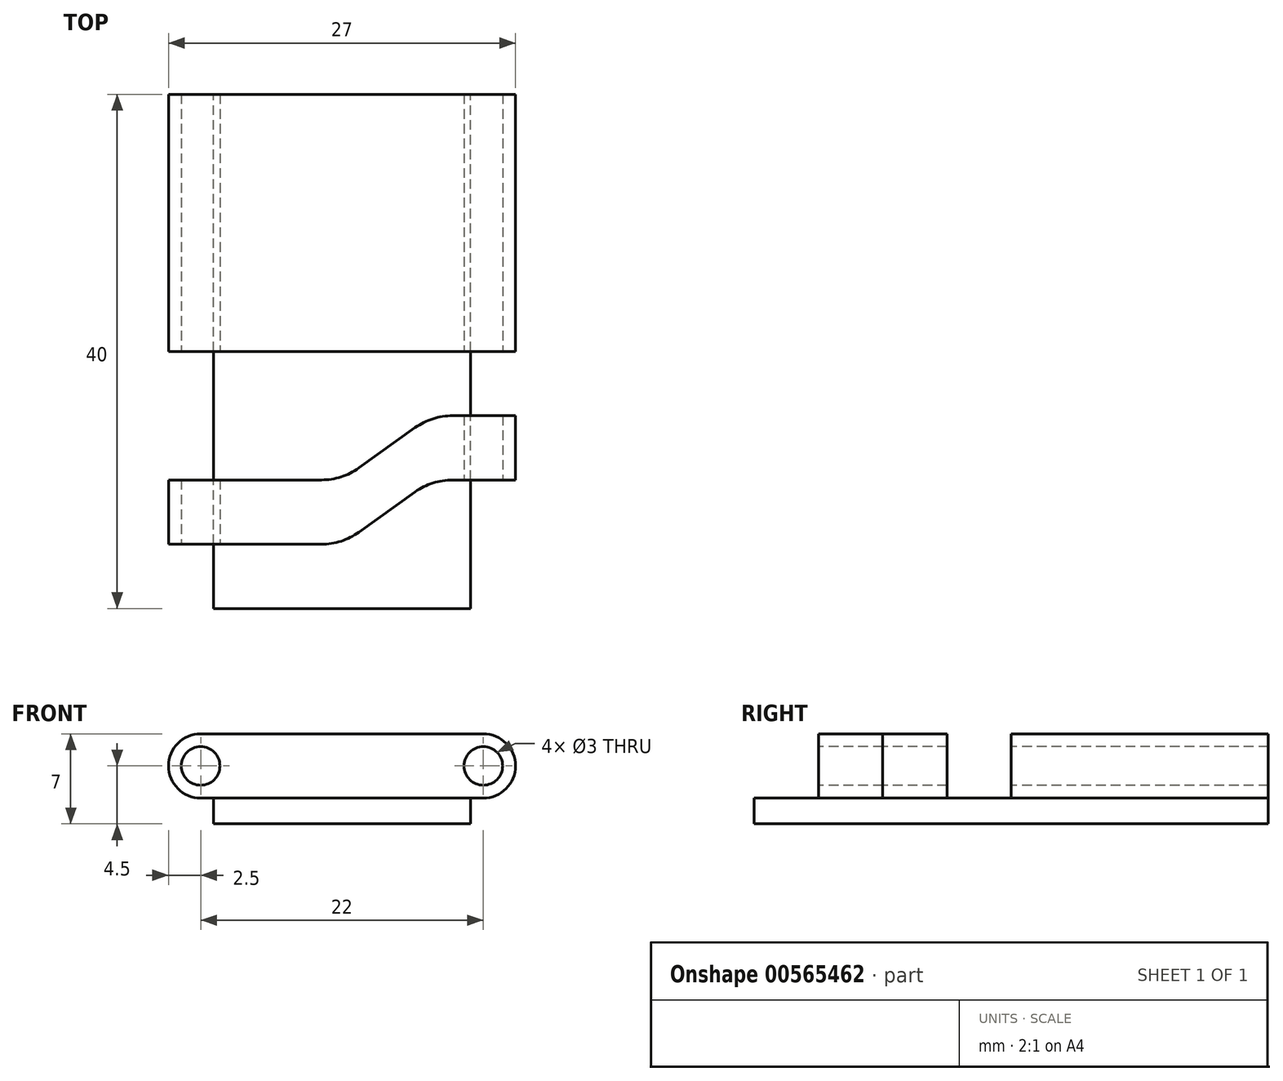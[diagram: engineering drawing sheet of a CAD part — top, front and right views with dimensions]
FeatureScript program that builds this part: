
annotation { "Feature Type Name" : "Feature", "Feature Type Description" : "" }
export const myFeature = defineFeature(function(context is Context, id is Id, definition is map)
    precondition{}
    {
        {
            var Q0;
            Q0=qCreatedBy(makeId("Front.planeOp"),FACE);
            var sketch = newSketch(context, id + "F0", { "sketchPlane" : qUnion([Q0])});
            skLineSegment(sketch, "E0.bottom", {"start": v(-10, 0) * mm, "end": v(10, 0) * mm});
            skLineSegment(sketch, "E0.top", {"start": v(-10, -1) * mm, "end": v(10, -1) * mm});
            skLineSegment(sketch, "E0.left", {"start": v(-10, 0) * mm, "end": v(-10, -1) * mm});
            skLineSegment(sketch, "E0.right", {"start": v(10, 0) * mm, "end": v(10, -1) * mm});
            skPoint(sketch, "E1", {"position": v(0, 0) * mm});
            skSolve(sketch);
        }
        {
            var Q0;
            Q0 = qSketchRegion(id + "F0", true);
            extrude(context, id + "F1", {"entities" : qUnion([Q0]), "depth" : 20 * mm, "offsetDistance" : 25 * mm, "hasSecondDirection" : true, "secondDirectionOppositeDirection" : true, "secondDirectionDepth" : 20 * mm});
        }
        {
            var Q0;
            Q0=makeQuery(id+"F1.opExtrude","CAP_FACE",FACE,{"disambiguationData":[OSD([sQuery(id+"F0.wireOp",EDGE,"E0.bottom"),sQuery(id+"F0.wireOp",EDGE,"E0.top"),sQuery(id+"F0.wireOp",EDGE,"E0.left"),sQuery(id+"F0.wireOp",EDGE,"E0.right")])],"isStart":true});
            var sketch = newSketch(context, id + "F2", { "sketchPlane" : qUnion([Q0])});
            skArc(sketch, "E2", {"start": v(11, 1) * mm, "mid": v(13.5, 3.5) * mm, "end": v(11, 6) * mm});
            skLineSegment(sketch, "E3", {"start": v(11, 1) * mm, "end": v(10, 1) * mm});
            skLineSegment(sketch, "E4", {"start": v(10, 1) * mm, "end": v(10, 0) * mm});
            skLineSegment(sketch, "E5", {"start": v(11, 3.5) * mm, "end": v(11, 1) * mm, "construction": true});
            skLineSegment(sketch, "E6", {"start": v(11, 6) * mm, "end": v(0, 6) * mm});
            skLineSegment(sketch, "E7", {"start": v(11, 3.5) * mm, "end": v(11, 6) * mm, "construction": true});
            skLineSegment(sketch, "E8", {"start": v(0, 0) * mm, "end": v(0, 10.25) * mm, "construction": true});
            skLineSegment(sketch, "E9", {"start": v(0, 0) * mm, "end": v(10, 0) * mm});
            skLineSegment(sketch, "E10.MirrorCS", {"start": v(-11, 6) * mm, "end": v(0, 6) * mm});
            skLineSegment(sketch, "E11.MirrorCS", {"start": v(-11, 3.5) * mm, "end": v(-11, 1) * mm, "construction": true});
            skLineSegment(sketch, "E12.MirrorCS", {"start": v(-11, 3.5) * mm, "end": v(-11, 6) * mm, "construction": true});
            skLineSegment(sketch, "E13.MirrorCS", {"start": v(0, 0) * mm, "end": v(-10, 0) * mm});
            skLineSegment(sketch, "E14.MirrorCS", {"start": v(-11, 1) * mm, "end": v(-10, 1) * mm});
            skLineSegment(sketch, "E15.MirrorCS", {"start": v(-10, 1) * mm, "end": v(-10, 0) * mm});
            skArc(sketch, "E16.MirrorCS", {"start": v(-11, 1) * mm, "mid": v(-13.5, 3.5) * mm, "end": v(-11, 6) * mm});
            skSolve(sketch);
        }
        {
            var Q0;
            Q0 = qSketchRegion(id + "F2", true);
            var Q1;
            Q1=makeQuery(id+"F1.opExtrude","CAP_FACE",FACE,{"disambiguationData":[OSD([sQuery(id+"F0.wireOp",EDGE,"E0.bottom"),sQuery(id+"F0.wireOp",EDGE,"E0.top"),sQuery(id+"F0.wireOp",EDGE,"E0.left"),sQuery(id+"F0.wireOp",EDGE,"E0.right")])],"isStart":false});
            extrude(context, id + "F3", {"entities" : qUnion([Q0]), "operationType" : NewBodyOperationType.ADD, "endBound" : BoundingType.UP_TO_SURFACE, "oppositeDirection" : true, "depth" : 25 * mm, "endBoundEntityFace" : qUnion([Q1]), "offsetDistance" : 25 * mm});
        }
        {
            var Q0;
            Q0=makeQuery(id+"F3.opExtrude","SWEPT_FACE",FACE,{"disambiguationData":[OSD([sQuery(id+"F2.wireOp",EDGE,"E6"),sQuery(id+"F2.wireOp",EDGE,"E10.MirrorCS")])]});
            var sketch = newSketch(context, id + "F4", { "sketchPlane" : qUnion([Q0])});
            skLineSegment(sketch, "E17", {"start": v(-19.6, 0) * mm, "end": v(21.58, 0) * mm, "construction": true});
            skPoint(sketch, "E17.endSnap0", {"position": v(-11, 0) * mm});
            skLineSegment(sketch, "E18", {"start": v(-16.8, -15) * mm, "end": v(16.67, -15) * mm, "construction": true});
            skPoint(sketch, "E19.0", {"position": v(-13.5, -20) * mm});
            skPoint(sketch, "E20.0", {"position": v(13.5, -20) * mm});
            skLineSegment(sketch, "E21", {"start": v(-13.5, -20) * mm, "end": v(-13.5, 0) * mm, "construction": true});
            skLineSegment(sketch, "E22", {"start": v(13.5, -20) * mm, "end": v(13.5, 0) * mm, "construction": true});
            skPoint(sketch, "E23", {"position": v(-13.5, -15) * mm});
            skPoint(sketch, "E24", {"position": v(13.5, -15) * mm});
            skLineSegment(sketch, "E25", {"start": v(-13.5, -15) * mm, "end": v(0, -15) * mm});
            skLineSegment(sketch, "E26", {"start": v(0, -15) * mm, "end": v(7, -10) * mm});
            skLineSegment(sketch, "E27", {"start": v(7, -10) * mm, "end": v(13.5, -10) * mm});
            skLineSegment(sketch, "E28", {"start": v(-13.5, -15) * mm, "end": v(-13.5, -20) * mm});
            skLineSegment(sketch, "E29", {"start": v(13.5, -20) * mm, "end": v(13.5, -10) * mm});
            skLineSegment(sketch, "E30", {"start": v(-13.5, -10) * mm, "end": v(0, -10) * mm});
            skLineSegment(sketch, "E31", {"start": v(0, -10) * mm, "end": v(7, -5) * mm});
            skLineSegment(sketch, "E32", {"start": v(7, -5) * mm, "end": v(13.5, -5) * mm});
            skLineSegment(sketch, "E33", {"start": v(-13.5, -10) * mm, "end": v(-13.5, 0) * mm});
            skLineSegment(sketch, "E34", {"start": v(-13.5, 0) * mm, "end": v(17.6, 0) * mm});
            skLineSegment(sketch, "E35", {"start": v(17.6, 0) * mm, "end": v(13.5, 0) * mm});
            skLineSegment(sketch, "E36", {"start": v(13.5, -5) * mm, "end": v(13.5, 0) * mm});
            skLineSegment(sketch, "E37", {"start": v(-13.5, -20) * mm, "end": v(13.5, -20) * mm});
            skSolve(sketch);
        }
        {
            var Q0;
            Q0 = qSketchRegion(id + "F4", true);
            var Q1;
            Q1=makeQuery(id+"F3.opExtrude","CAP_VERTEX",VERTEX,{"disambiguationData":[OSD([sQuery(id+"F0.wireOp",EDGE,"E0.bottom"),sQuery(id+"F0.wireOp",EDGE,"E0.top"),sQuery(id+"F0.wireOp",EDGE,"E0.left"),sQuery(id+"F0.wireOp",EDGE,"E0.right"),sQuery(id+"F2.wireOp",EDGE,"E3"),sQuery(id+"F2.wireOp",EDGE,"E4")])],"isStart":false});
            extrude(context, id + "F5", {"entities" : qUnion([Q0]), "operationType" : NewBodyOperationType.REMOVE, "endBound" : BoundingType.UP_TO_VERTEX, "oppositeDirection" : true, "depth" : 25 * mm, "endBoundEntityVertex" : qUnion([Q1]), "offsetDistance" : 25 * mm});
        }
        {
            var Q0;
            Q0=makeQuery(id+"F5.boolean.opBoolean","COPY",FACE,{"derivedFrom":makeQuery(id+"F5.opExtrude","SWEPT_FACE",FACE,{"disambiguationData":[OSD([sQuery(id+"F4.wireOp",EDGE,"E34")])]})});
            cPlane(context, id + "F6", {"entities" : qUnion([Q0]), "cplaneType" : CPlaneType.OFFSET, "offset" : 0 * mm, "width" : 150 * mm, "height" : 150 * mm});
        }
        {
            var Q0;
            Q0=qCreatedBy(id+"F6.planeOp",FACE);
            var sketch = newSketch(context, id + "F7", { "sketchPlane" : qUnion([Q0])});
            skArc(sketch, "E38.0", {"start": v(11, 1) * mm, "mid": v(13.5, 3.5) * mm, "end": v(11, 6) * mm, "construction": true});
            skArc(sketch, "E38.1", {"start": v(-11, 1) * mm, "mid": v(-13.5, 3.5) * mm, "end": v(-11, 6) * mm, "construction": true});
            skCircle(sketch, "E39", {"center": v(11, 3.5) * mm, "radius": 1.5 * mm});
            skCircle(sketch, "E40.MirrorC", {"center": v(-11, 3.5) * mm, "radius": 1.5 * mm});
            skSolve(sketch);
        }
        {
            var Q0;
            Q0 = qSketchRegion(id + "F7", true);
            extrude(context, id + "F8", {"entities" : qUnion([Q0]), "operationType" : NewBodyOperationType.REMOVE, "endBound" : BoundingType.THROUGH_ALL, "oppositeDirection" : true, "depth" : 25 * mm, "offsetDistance" : 25 * mm, "hasSecondDirection" : true, "secondDirectionBound" : SecondDirectionBoundingType.THROUGH_ALL, "secondDirectionOppositeDirection" : false, "secondDirectionDepth" : 25 * mm});
        }
        {
            var Q0;
            Q0=makeQuery(id+"F5.boolean.opBoolean","COPY",EDGE,{"derivedFrom":makeQuery(id+"F5.opExtrude","SWEPT_EDGE",EDGE,{"disambiguationData":[OSD([sQuery(id+"F4.wireOp",EDGE,"E25"),sQuery(id+"F4.wireOp",EDGE,"E26")])]})});
            var Q1;
            Q1=makeQuery(id+"FyR8BB6THSKzxIG_1.1.F5.boolean.opBoolean","COPY",EDGE,{"derivedFrom":makeQuery(id+"FyR8BB6THSKzxIG_1.1.F5.opExtrude","SWEPT_EDGE",EDGE,{"disambiguationData":[OSD([sQuery(id+"F4.wireOp",EDGE,"E30"),sQuery(id+"F4.wireOp",EDGE,"E31")])]})});
            var Q2;
            Q2=makeQuery(id+"FyR8BB6THSKzxIG_1.1.F5.boolean.opBoolean","COPY",EDGE,{"derivedFrom":makeQuery(id+"FyR8BB6THSKzxIG_1.1.F5.opExtrude","SWEPT_EDGE",EDGE,{"disambiguationData":[OSD([sQuery(id+"F4.wireOp",EDGE,"E26"),sQuery(id+"F4.wireOp",EDGE,"E27")])]})});
            var Q3;
            Q3=makeQuery(id+"FyR8BB6THSKzxIG_1.1.F5.boolean.opBoolean","COPY",EDGE,{"derivedFrom":makeQuery(id+"FyR8BB6THSKzxIG_1.1.F5.opExtrude","SWEPT_EDGE",EDGE,{"disambiguationData":[OSD([sQuery(id+"F4.wireOp",EDGE,"E25"),sQuery(id+"F4.wireOp",EDGE,"E26")])]})});
            var Q4;
            Q4=makeQuery(id+"F5.boolean.opBoolean","COPY",EDGE,{"derivedFrom":makeQuery(id+"F5.opExtrude","SWEPT_EDGE",EDGE,{"disambiguationData":[OSD([sQuery(id+"F4.wireOp",EDGE,"E30"),sQuery(id+"F4.wireOp",EDGE,"E31")])]})});
            var Q5;
            Q5=makeQuery(id+"F5.boolean.opBoolean","COPY",EDGE,{"derivedFrom":makeQuery(id+"F5.opExtrude","SWEPT_EDGE",EDGE,{"disambiguationData":[OSD([sQuery(id+"F4.wireOp",EDGE,"E31"),sQuery(id+"F4.wireOp",EDGE,"E32")])]})});
            var Q6;
            Q6=makeQuery(id+"F5.boolean.opBoolean","COPY",EDGE,{"derivedFrom":makeQuery(id+"F5.opExtrude","SWEPT_EDGE",EDGE,{"disambiguationData":[OSD([sQuery(id+"F4.wireOp",EDGE,"E26"),sQuery(id+"F4.wireOp",EDGE,"E27")])]})});
            var Q7;
            Q7=makeQuery(id+"FyR8BB6THSKzxIG_1.1.F5.boolean.opBoolean","COPY",EDGE,{"derivedFrom":makeQuery(id+"FyR8BB6THSKzxIG_1.1.F5.opExtrude","SWEPT_EDGE",EDGE,{"disambiguationData":[OSD([sQuery(id+"F4.wireOp",EDGE,"E31"),sQuery(id+"F4.wireOp",EDGE,"E32")])]})});
            fillet(context, id + "F9", {"entities" : qUnion([Q0, Q1, Q2, Q3, Q4, Q5, Q6, Q7]), "radius" : 5 * mm, "tangentPropagation" : true, "allowEdgeOverflow" : false});
        }
    });
